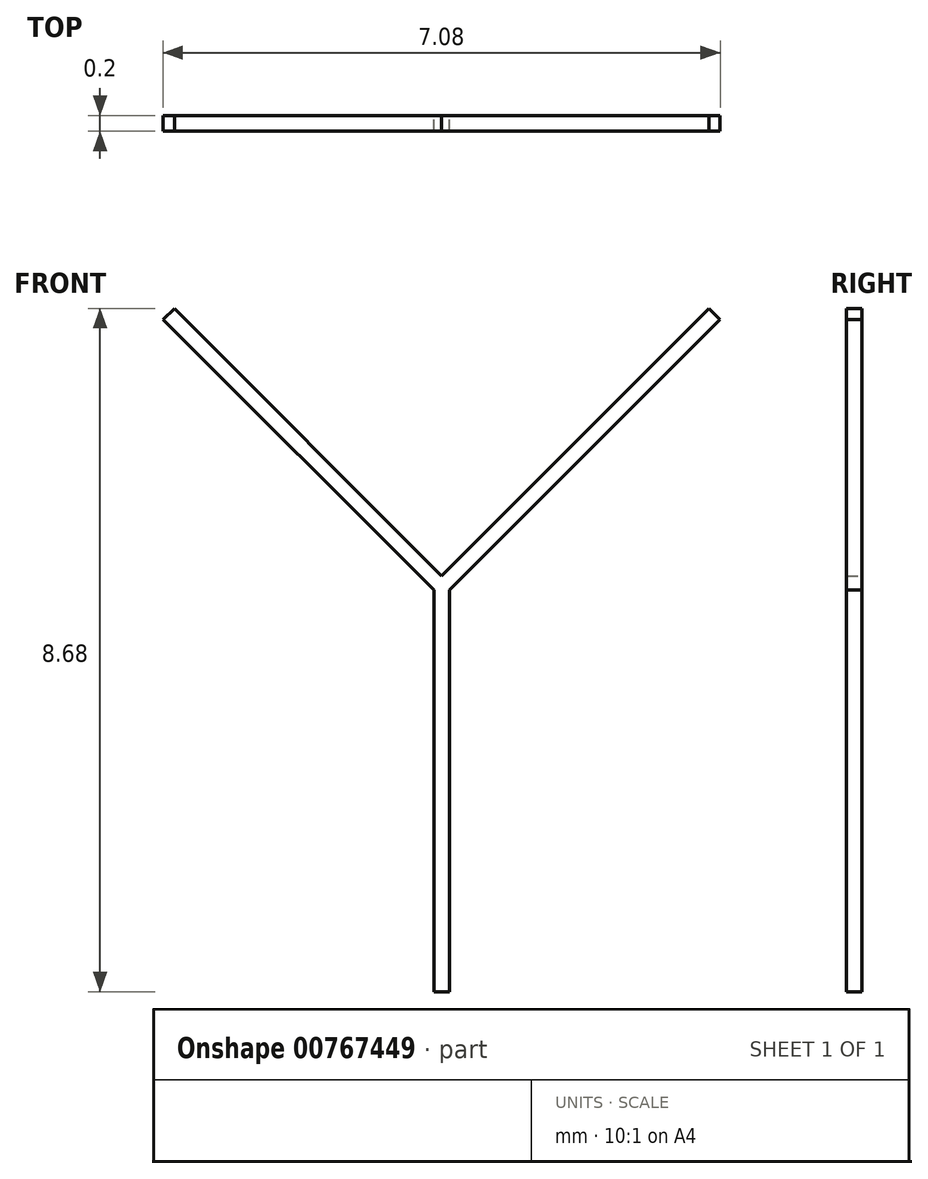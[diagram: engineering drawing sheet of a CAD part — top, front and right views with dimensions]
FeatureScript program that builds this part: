
annotation { "Feature Type Name" : "Feature", "Feature Type Description" : "" }
export const myFeature = defineFeature(function(context is Context, id is Id, definition is map)
    precondition{}
    {
        {
            var Q0;
            Q0=qCreatedBy(makeId("Front.planeOp"),FACE);
            var sketch = newSketch(context, id + "F0", { "sketchPlane" : qUnion([Q0])});
            skLineSegment(sketch, "E0", {"start": v(-3.54, 3.54) * mm, "end": v(-0.1, 0.1) * mm});
            skLineSegment(sketch, "E1", {"start": v(0.1, 0.1) * mm, "end": v(3.54, 3.54) * mm});
            skLineSegment(sketch, "E2.0", {"start": v(-3.4, 3.68) * mm, "end": v(0, 0.28) * mm});
            skLineSegment(sketch, "E3.0", {"start": v(0, 0.28) * mm, "end": v(3.4, 3.68) * mm});
            skLineSegment(sketch, "E4.0", {"start": v(0.1, 0.1) * mm, "end": v(0.1, -5) * mm});
            skLineSegment(sketch, "E5.0", {"start": v(-0.1, 0.1) * mm, "end": v(-0.1, -5) * mm});
            skLineSegment(sketch, "E6", {"start": v(-0.1, -5) * mm, "end": v(0.1, -5) * mm});
            skLineSegment(sketch, "E7", {"start": v(-3.4, 3.68) * mm, "end": v(-3.54, 3.54) * mm});
            skLineSegment(sketch, "E8", {"start": v(3.54, 3.54) * mm, "end": v(3.4, 3.68) * mm});
            skSolve(sketch);
        }
        {
            var Q0;
            Q0 = qSketchRegion(id + "F0", true);
            extrude(context, id + "F1", {"entities" : qUnion([Q0]), "depth" : 0.2 * mm, "offsetDistance" : 25 * mm});
        }
    });
